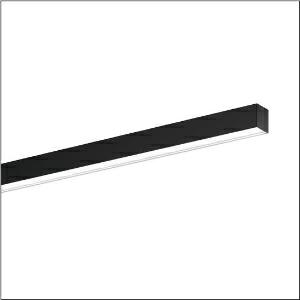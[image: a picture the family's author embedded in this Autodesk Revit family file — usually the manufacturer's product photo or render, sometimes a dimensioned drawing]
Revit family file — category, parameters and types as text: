
# Revit family: silica_r__21_51mx23dc3abb_3531
name_source: partatom
category: Lighting Fixtures
units: mm (PartAtom-declared; Revit-internal decimal feet)

## family parameters
Cut with Voids When Loaded = No
Host = Face
Light Source = No
Part Type = Normal
Room Calculation Point = No
Round Connector Dimension = Use Diameter
Shared = No

## types (1)
- --- (1 x LED, 8200 lm, 62.2 W, 3000K)
    Apparent Load = 62 VA
    CIE Flux Codes = 78 96 99 100 100
    Color Rendering = 80
    Color Temperature = 3000K
    Default Elevation = 1800 mm
    Description = Silica® 21, office luminaire, primary optical cover: prismatic diffuser, of PMMA, CAT 2 (L<= 3000cd/m²), light emission: direct distribution, primary light characteristic: symmetric, installation type: surface-mounted, LED, rated luminous flux: 8.200lm, luminous efficacy: 132lm/W, light colour: 830, colour temperature: 3000K, with terminal, 3+2-pole, max. 2.5mm², mains connection: 220..240V, AC, 50/60Hz, rated input power: 62.2W, luminaire housing, of aluminium, jet black (RAL 9005), length: 3.004mm, width: 53mm, height: 53mm, protection rating (complete): IP20, insulation class (complete): insulation class I (protective earthing), certification: CE, permissible operating ambient temperature: 0..+35°C, standard: EN 50419, packaging unit: 1 piece
    Height = 0 mm  [stored 0 ft]
    Lamp = 1 x LED
    Lamp Light Flux = 8200 lm
    Lamp Power = 62.2 W
    Lamp count = 1
    Length = 3004 mm
    Luminous efficacy = 132 lm/W
    Manufacturer = Siteco
    ModVariant = No
    Model = 51MX23DC3ABB
    Mounting Place = Ceiling
    Mounting Type = Recessed
    Number of Poles = 1
    OnlyDefault = Yes
    Power Factor = 1
    Product Name = Silica® 21
    Product group = office luminaire | ceiling recessed
    ProductGroupID = 401
    Protection Class = Protection class I
    Protection Degree = IP 20
    RLX_Detail_Level = 1
    RLX_Emergency_Light_Flux = 0 lm
    RLX_Emergency_Type = 0
    RLX_Emergency_Type_DB = No
    RlxData = <blob elided: 23677 chars, md5=f82e7f63>
    Socket = socket
    Standby Power = 0 W
    System Light Flux = 8200 lm
    System Power = 62 W
    Type Comments = factory setting: luminous flux: 100 % | dim-lin: 254 | 345 mA
    Type Image = l_1313584.jpg
    URL = http://relux.com
    VarID = @adj_067981
    Voltage = 0 V
    Weight = 0.00 kg
    Width = 53 mm

note: [stored X ft] marks values corroborated as IEEE doubles in the binary element streams (Revit-internal decimal feet)

## geometry (parser evidence)
native form markers: Blend x4, Sweep x9
no freeform markers — native parametric forms only
